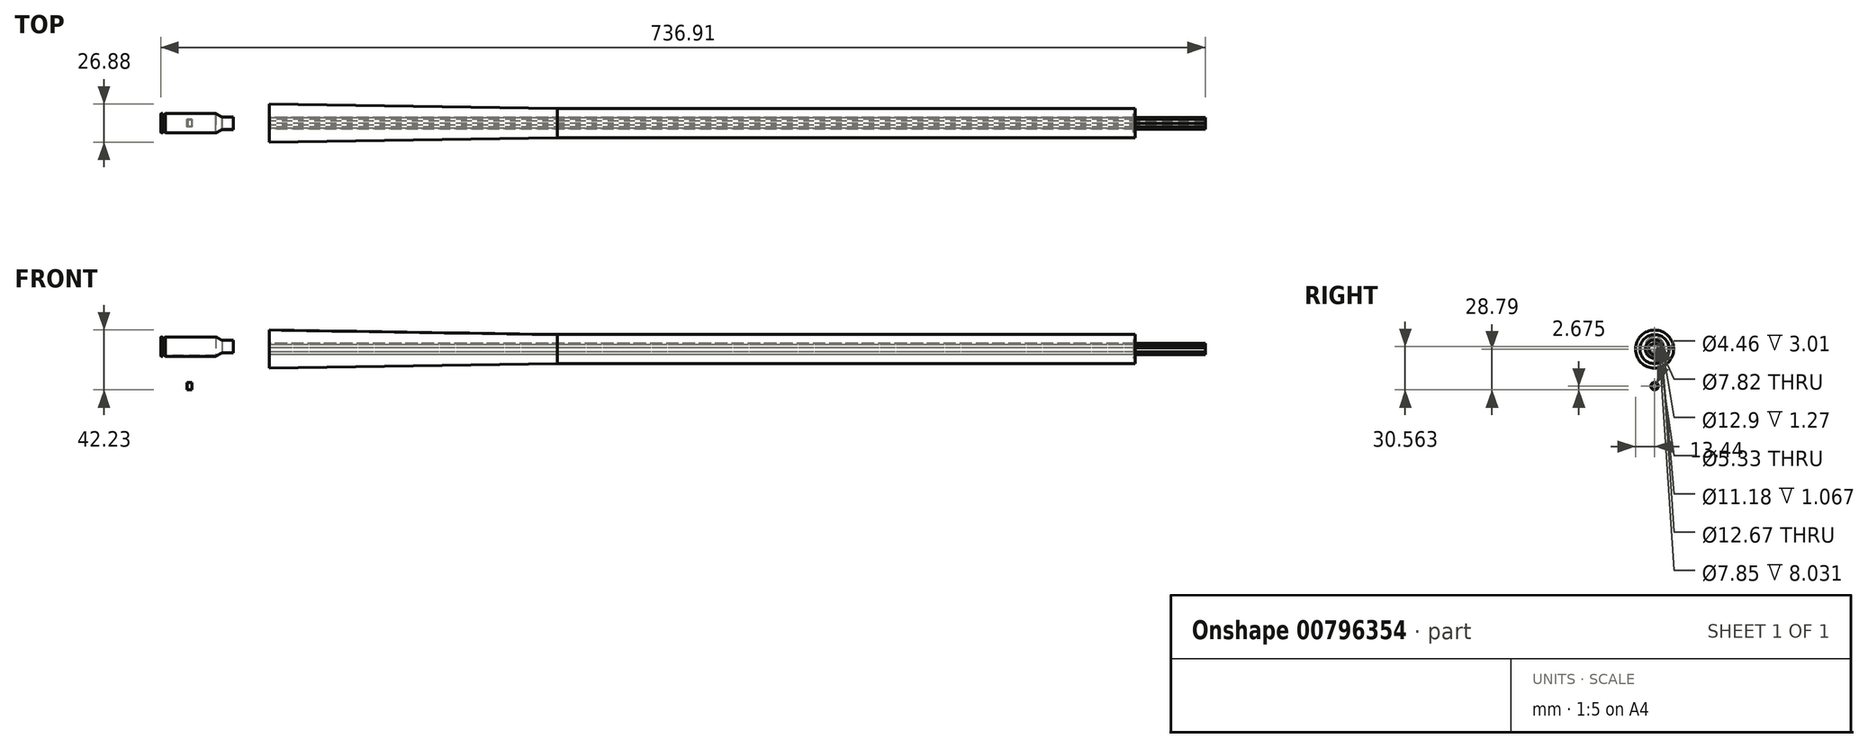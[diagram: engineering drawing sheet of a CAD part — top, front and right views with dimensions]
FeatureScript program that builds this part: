
annotation { "Feature Type Name" : "Feature", "Feature Type Description" : "" }
export const myFeature = defineFeature(function(context is Context, id is Id, definition is map)
    precondition{}
    {
        {
            var Q0;
            Q0=qCreatedBy(makeId("Front.planeOp"),FACE);
            var sketch = newSketch(context, id + "F0", { "sketchPlane" : qUnion([Q0])});
            skLineSegment(sketch, "E0", {"start": v(-76.5, 1.77) * mm, "end": v(28.95, 1.77) * mm, "construction": true});
            skLineSegment(sketch, "E1", {"start": v(-76.5, 4.44) * mm, "end": v(-76.5, 8.27) * mm});
            skLineSegment(sketch, "E2", {"start": v(-76.5, 8.27) * mm, "end": v(-76.1, 8.55) * mm});
            skLineSegment(sketch, "E3", {"start": v(-75.24, 8.55) * mm, "end": v(-75.24, 7.8) * mm});
            skLineSegment(sketch, "E4", {"start": v(-75.24, 7.8) * mm, "end": v(-74.3, 7.8) * mm});
            skLineSegment(sketch, "E5", {"start": v(-73.1, 8.55) * mm, "end": v(-74.3, 7.8) * mm});
            skLineSegment(sketch, "E6", {"start": v(-76.1, 8.55) * mm, "end": v(-75.24, 8.55) * mm});
            skLineSegment(sketch, "E7", {"start": v(-73.1, 8.55) * mm, "end": v(-37.43, 8.55) * mm});
            skLineSegment(sketch, "E8", {"start": v(-37.43, 8.55) * mm, "end": v(-33.24, 6.14) * mm});
            skLineSegment(sketch, "E9", {"start": v(-33.24, 6.14) * mm, "end": v(-25.33, 6.14) * mm});
            skLineSegment(sketch, "E10.0", {"start": v(-33.36, 5.7) * mm, "end": v(-25.33, 5.7) * mm});
            skLineSegment(sketch, "E11.0", {"start": v(-37.55, 8.11) * mm, "end": v(-33.36, 5.7) * mm});
            skLineSegment(sketch, "E12.0", {"start": v(-72.97, 8.11) * mm, "end": v(-37.55, 8.11) * mm});
            skLineSegment(sketch, "E13.0", {"start": v(-72.97, 8.11) * mm, "end": v(-74.17, 7.36) * mm});
            skLineSegment(sketch, "E14.0", {"start": v(-75.24, 7.36) * mm, "end": v(-74.17, 7.36) * mm});
            skLineSegment(sketch, "E15", {"start": v(-75.24, 7.36) * mm, "end": v(-75.24, 4.44) * mm});
            skLineSegment(sketch, "E16", {"start": v(-25.33, 6.14) * mm, "end": v(-25.33, 5.7) * mm});
            skLineSegment(sketch, "E17.0", {"start": v(-76.5, 4.44) * mm, "end": v(-75.24, 4.44) * mm});
            skSolve(sketch);
        }
        {
            var Q0;
            Q0=makeQuery(id+"F0.imprint","IMPRINT",FACE,{"disambiguationData":[TD([[makeQuery(id+"F0.imprint","IMPRINT",EDGE,{"derivedFrom":sQuery(id+"F0.wireOp",EDGE,"E1")}),-1.0]])]});
            var Q1;
            Q1=sQuery(id+"F0.wireOp",EDGE,"E1");
            var Q2;
            Q2=sQuery(id+"F0.wireOp",EDGE,"E7");
            var Q3;
            Q3=sQuery(id+"F0.wireOp",EDGE,"E5");
            var Q4;
            Q4=sQuery(id+"F0.wireOp",EDGE,"E8");
            var Q5;
            Q5=sQuery(id+"F0.wireOp",EDGE,"E9");
            var Q6;
            Q6=sQuery(id+"F0.wireOp",EDGE,"E4");
            var Q7;
            Q7=sQuery(id+"F0.wireOp",EDGE,"E3");
            var Q8;
            Q8=sQuery(id+"F0.wireOp",EDGE,"E6");
            var Q9;
            Q9=sQuery(id+"F0.wireOp",EDGE,"E2");
            var Q10;
            Q10=sQuery(id+"F0.wireOp",EDGE,"E15");
            var Q11;
            Q11=sQuery(id+"F0.wireOp",EDGE,"E14.0");
            var Q12;
            Q12=sQuery(id+"F0.wireOp",EDGE,"E13.0");
            var Q13;
            Q13=sQuery(id+"F0.wireOp",EDGE,"E12.0");
            var Q14;
            Q14=sQuery(id+"F0.wireOp",EDGE,"E11.0");
            var Q15;
            Q15=sQuery(id+"F0.wireOp",EDGE,"E10.0");
            var Q16;
            Q16=sQuery(id+"F0.wireOp",EDGE,"E16");
            var Q17;
            Q17=sQuery(id+"F0.wireOp",EDGE,"E17.0");
            var Q18;
            Q18=sQuery(id+"F0.wireOp",EDGE,"E0");
            revolve(context, id + "F1", {"surfaceOperationType" : NewSurfaceOperationType.NEW, "entities" : qUnion([Q0]), "surfaceEntities" : qUnion([Q1, Q2, Q3, Q4, Q5, Q6, Q7, Q8, Q9, Q10, Q11, Q12, Q13, Q14, Q15, Q16, Q17]), "axis" : qUnion([Q18]), "revolveType" : RevolveType.FULL});
        }
        {
            var Q0;
            Q0=makeQuery(id+"F1.opRevolve","SWEPT_EDGE",EDGE,{"disambiguationData":[OSD([sQuery(id+"F0.wireOp",VERTEX,"E9.start")])]});
            var Q1;
            Q1=makeQuery(id+"F1.opRevolve","SWEPT_EDGE",EDGE,{"disambiguationData":[OSD([sQuery(id+"F0.wireOp",EDGE,"E8"),sQuery(id+"F0.wireOp",EDGE,"E9")])]});
            fillet(context, id + "F2", {"entities" : qUnion([Q0, Q1]), "radius" : 3.17 * mm, "tangentPropagation" : true, "allowEdgeOverflow" : false});
        }
        {
            var Q0;
            Q0=makeQuery(id+"F1.opRevolve","SWEPT_EDGE",EDGE,{"disambiguationData":[OSD([sQuery(id+"F0.wireOp",VERTEX,"E8.start")])]});
            var Q1;
            Q1=makeQuery(id+"F1.opRevolve","SWEPT_EDGE",EDGE,{"disambiguationData":[OSD([sQuery(id+"F0.wireOp",EDGE,"E7"),sQuery(id+"F0.wireOp",EDGE,"E8")])]});
            fillet(context, id + "F3", {"entities" : qUnion([Q0, Q1]), "radius" : 0.76 * mm, "tangentPropagation" : true, "allowEdgeOverflow" : false});
        }
        {
            var Q0;
            Q0=makeQuery(id+"F1.opRevolve","SWEPT_EDGE",EDGE,{"disambiguationData":[OSD([sQuery(id+"F0.wireOp",VERTEX,"E17.0.start")])]});
            var Q1;
            Q1=makeQuery(id+"F1.opRevolve","SWEPT_EDGE",EDGE,{"disambiguationData":[OSD([sQuery(id+"F0.wireOp",EDGE,"E1"),sQuery(id+"F0.wireOp",EDGE,"E17.0")])]});
            fillet(context, id + "F4", {"entities" : qUnion([Q0, Q1]), "radius" : 0.38 * mm, "tangentPropagation" : true, "allowEdgeOverflow" : false});
        }
        {
            var Q0;
            Q0=qCreatedBy(makeId("Front.planeOp"),FACE);
            var sketch = newSketch(context, id + "F5", { "sketchPlane" : qUnion([Q0])});
            skLineSegment(sketch, "E18", {"start": v(-57.94, -26.11) * mm, "end": v(-50.39, -26.11) * mm, "construction": true});
            skLineSegment(sketch, "E19", {"start": v(-57.94, -26.11) * mm, "end": v(-57.94, -23.44) * mm});
            skLineSegment(sketch, "E20", {"start": v(-57.94, -23.44) * mm, "end": v(-54.48, -23.44) * mm});
            skLineSegment(sketch, "E21.0", {"start": v(-57.5, -23.89) * mm, "end": v(-54.48, -23.89) * mm});
            skLineSegment(sketch, "E22.0", {"start": v(-57.5, -26.11) * mm, "end": v(-57.5, -23.89) * mm});
            skLineSegment(sketch, "E23", {"start": v(-54.48, -23.44) * mm, "end": v(-54.48, -23.89) * mm});
            skLineSegment(sketch, "E24", {"start": v(-57.94, -26.11) * mm, "end": v(-57.5, -26.11) * mm});
            skSolve(sketch);
        }
        {
            var Q0;
            Q0=makeQuery(id+"F5.imprint","IMPRINT",FACE,{"disambiguationData":[TD([[makeQuery(id+"F5.imprint","IMPRINT",EDGE,{"derivedFrom":sQuery(id+"F5.wireOp",EDGE,"E19")}),-1.0]])]});
            var Q1;
            Q1=sQuery(id+"F5.wireOp",EDGE,"E20");
            var Q2;
            Q2=sQuery(id+"F5.wireOp",EDGE,"E23");
            var Q3;
            Q3=sQuery(id+"F5.wireOp",EDGE,"E21.0");
            var Q4;
            Q4=sQuery(id+"F5.wireOp",EDGE,"E22.0");
            var Q5;
            Q5=sQuery(id+"F5.wireOp",EDGE,"E19");
            var Q6;
            Q6=sQuery(id+"F5.wireOp",EDGE,"E18");
            revolve(context, id + "F6", {"surfaceOperationType" : NewSurfaceOperationType.NEW, "entities" : qUnion([Q0]), "surfaceEntities" : qUnion([Q1, Q2, Q3, Q4, Q5]), "axis" : qUnion([Q6]), "revolveType" : RevolveType.FULL});
        }
        {
            var Q0;
            Q0=qCreatedBy(makeId("Front.planeOp"),FACE);
            var sketch = newSketch(context, id + "F7", { "sketchPlane" : qUnion([Q0])});
            skLineSegment(sketch, "E25", {"start": v(0, 0) * mm, "end": v(609.6, 0) * mm, "construction": true});
            skLineSegment(sketch, "E26.0", {"start": v(0, 3.91) * mm, "end": v(609.6, 3.91) * mm});
            skLineSegment(sketch, "E27.0", {"start": v(203.2, 10.26) * mm, "end": v(610.87, 10.26) * mm});
            skLineSegment(sketch, "E28", {"start": v(609.6, 3.91) * mm, "end": v(609.6, 6.45) * mm});
            skLineSegment(sketch, "E29", {"start": v(609.6, 6.45) * mm, "end": v(610.87, 6.45) * mm});
            skLineSegment(sketch, "E30", {"start": v(610.87, 6.45) * mm, "end": v(610.87, 10.26) * mm});
            skLineSegment(sketch, "E31", {"start": v(0, 3.91) * mm, "end": v(0, 13.44) * mm});
            skLineSegment(sketch, "E32", {"start": v(0, 13.44) * mm, "end": v(203.2, 10.26) * mm});
            skSolve(sketch);
        }
        {
            var Q0;
            Q0=makeQuery(id+"F7.imprint","IMPRINT",FACE,{"disambiguationData":[TD([[makeQuery(id+"F7.imprint","IMPRINT",EDGE,{"derivedFrom":sQuery(id+"F7.wireOp",EDGE,"E26.0")}),1.0]])]});
            var Q1;
            Q1=sQuery(id+"F7.wireOp",EDGE,"E25");
            revolve(context, id + "F8", {"surfaceOperationType" : NewSurfaceOperationType.NEW, "entities" : qUnion([Q0]), "axis" : qUnion([Q1]), "revolveType" : RevolveType.FULL});
        }
        {
            var Q0;
            Q0=qCreatedBy(makeId("Right.planeOp"),FACE);
            var sketch = newSketch(context, id + "F9", { "sketchPlane" : qUnion([Q0])});
            skCircle(sketch, "E33.cCircle", {"center": v(0, 0) * mm, "radius": 3.91 * mm, "construction": true});
            skLineSegment(sketch, "E33.0", {"start": v(1.42, -3.91) * mm, "end": v(-1.42, -3.91) * mm});
            skLineSegment(sketch, "E33.1", {"start": v(-1.42, -3.91) * mm, "end": v(-3.6, -2.08) * mm});
            skLineSegment(sketch, "E33.2", {"start": v(-3.6, -2.08) * mm, "end": v(-4.1, 0.72) * mm});
            skLineSegment(sketch, "E33.3", {"start": v(-4.1, 0.72) * mm, "end": v(-2.68, 3.19) * mm});
            skLineSegment(sketch, "E33.4", {"start": v(-2.68, 3.19) * mm, "end": v(0, 4.16) * mm});
            skLineSegment(sketch, "E33.5", {"start": v(0, 4.16) * mm, "end": v(2.68, 3.19) * mm});
            skLineSegment(sketch, "E33.6", {"start": v(2.68, 3.19) * mm, "end": v(4.1, 0.72) * mm});
            skLineSegment(sketch, "E33.7", {"start": v(4.1, 0.72) * mm, "end": v(3.6, -2.08) * mm});
            skLineSegment(sketch, "E33.8", {"start": v(3.6, -2.08) * mm, "end": v(1.42, -3.91) * mm});
            skPoint(sketch, "E33.0.midPoint", {"position": v(0, -3.91) * mm});
            skSolve(sketch);
        }
        {
            var Q0;
            Q0 = qSketchRegion(id + "F9", true);
            extrude(context, id + "F10", {"entities" : qUnion([Q0]), "depth" : 660.4 * mm, "offsetDistance" : 25.4 * mm});
        }
    });
